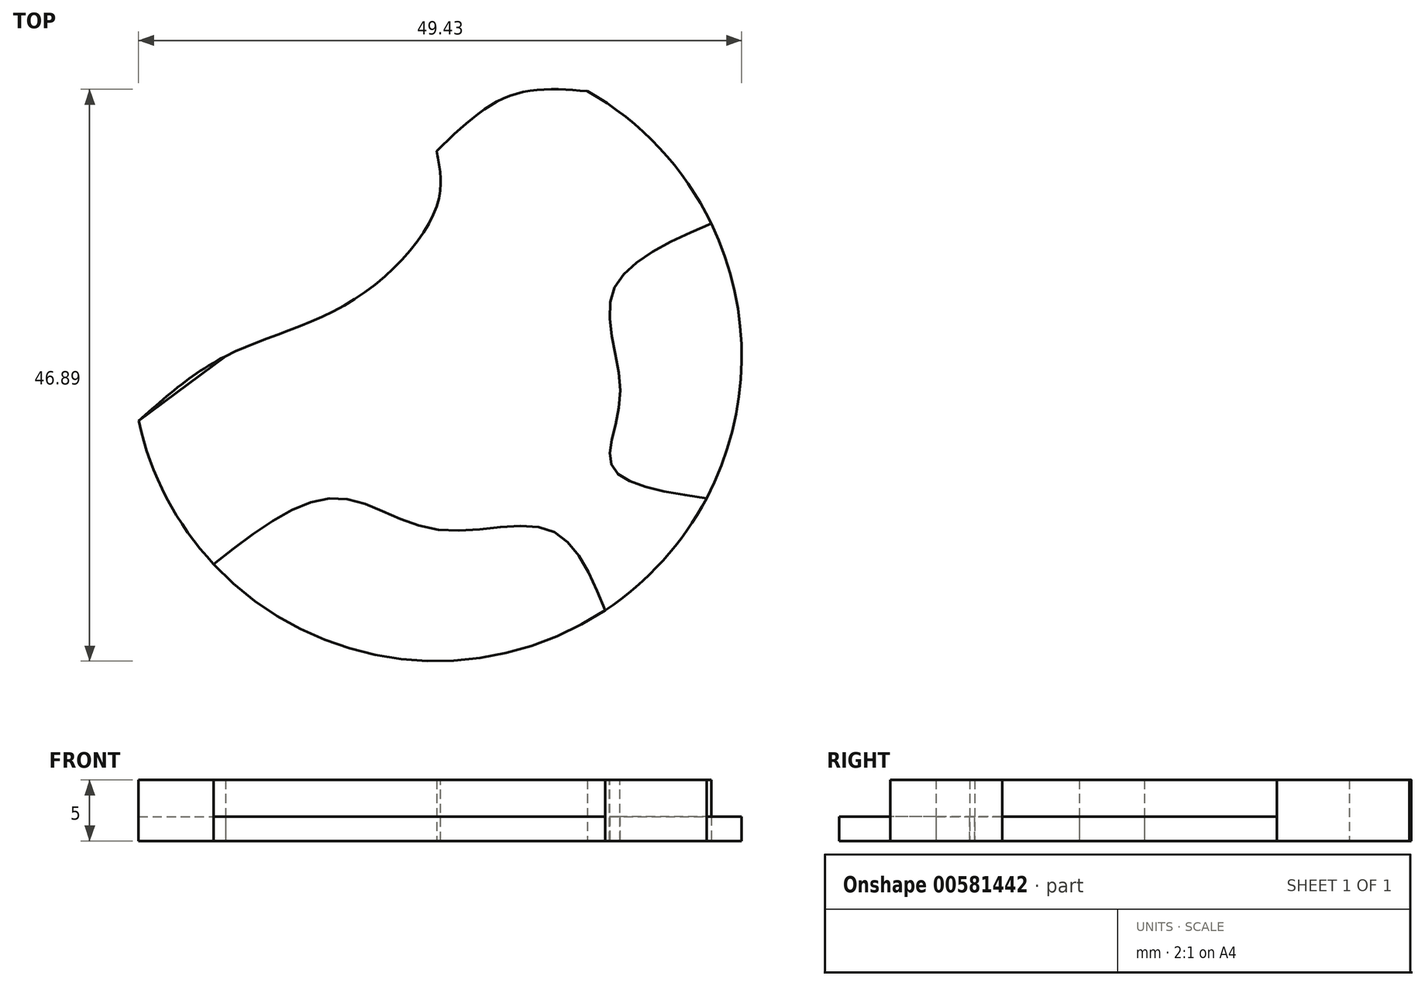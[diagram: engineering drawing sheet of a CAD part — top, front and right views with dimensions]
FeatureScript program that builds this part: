
annotation { "Feature Type Name" : "Feature", "Feature Type Description" : "" }
export const myFeature = defineFeature(function(context is Context, id is Id, definition is map)
    precondition{}
    {
        {
            var Q0;
            Q0=qCreatedBy(makeId("Top.planeOp"),FACE);
            var sketch = newSketch(context, id + "F0", { "sketchPlane" : qUnion([Q0])});
            skCircle(sketch, "E0", {"center": v(0, 0) * mm, "radius": 25 * mm});
            skLineSegment(sketch, "E1", {"start": v(-24.43, -5.32) * mm, "end": v(-17.3, 0) * mm});
            skLineSegment(sketch, "E2", {"start": v(0, 16.82) * mm, "end": v(0, 12.29) * mm});
            skFitSpline(sketch, "E3", {"points": [v(-24.43, -5.32) * mm, v(-17.3, 0) * mm, v(-6.95, 4.53) * mm, v(0, 12.29) * mm, v(0, 16.82) * mm], "startDerivative": vector(25.68, 23.1) * mm, "endDerivative": vector(-4.7, 23.42) * mm});
            skFitSpline(sketch, "E4", {"points": [v(0, 16.82) * mm, v(5.98, 21.34) * mm, v(12.35, 21.74) * mm], "startDerivative": vector(11.04, 10.75) * mm, "endDerivative": vector(13.68, -1.08) * mm});
            skFitSpline(sketch, "E5", {"points": [v(22.51, 10.87) * mm, v(14.4, 5.17) * mm, v(15.04, -3.23) * mm, v(14.4, -9.06) * mm, v(22.12, -11.65) * mm], "startDerivative": vector(-39.1, -16.9) * mm, "endDerivative": vector(41.16, -6) * mm});
            skFitSpline(sketch, "E6", {"points": [v(-18.27, -17.06) * mm, v(-8.25, -11.64) * mm, v(0, -14.23) * mm, v(9.22, -14.23) * mm, v(13.83, -20.83) * mm], "startDerivative": vector(37.27, 29.47) * mm, "endDerivative": vector(15.08, -36.88) * mm});
            skSolve(sketch);
        }
        {
            var Q0;
            {var subQ1=sQuery(id+"F0.wireOp",EDGE,"E1");Q0=makeQuery(id+"F0.imprint","IMPRINT",FACE,{"disambiguationData":[TD([[makeQuery(id+"F0.imprint","IMPRINT",EDGE,{"derivedFrom":subQ1}),1.0]])]});}
            var Q1;
            {var subQ0=sQuery(id+"F0.wireOp",EDGE,"E5");Q1=makeQuery(id+"F0.imprint","IMPRINT",FACE,{"disambiguationData":[TD([[makeQuery(id+"F0.imprint","IMPRINT",EDGE,{"derivedFrom":subQ0}),1.0]])]});}
            var Q2;
            {var subQ0=sQuery(id+"F0.wireOp",EDGE,"E6");Q2=makeQuery(id+"F0.imprint","IMPRINT",FACE,{"disambiguationData":[TD([[makeQuery(id+"F0.imprint","IMPRINT",EDGE,{"derivedFrom":subQ0}),-1.0]])]});}
            extrude(context, id + "F1", {"entities" : qUnion([Q0, Q1, Q2]), "depth" : 2 * mm, "offsetDistance" : 25 * mm});
        }
        {
            var Q0;
            {var subQ0=sQuery(id+"F0.wireOp",EDGE,"E1");Q0=makeQuery(id+"F0.imprint","IMPRINT",FACE,{"disambiguationData":[TD([[makeQuery(id+"F0.imprint","IMPRINT",EDGE,{"derivedFrom":subQ0}),-1.0]])]});}
            extrude(context, id + "F2", {"entities" : qUnion([Q0]), "depth" : 5 * mm, "offsetDistance" : 25 * mm});
        }
    });
